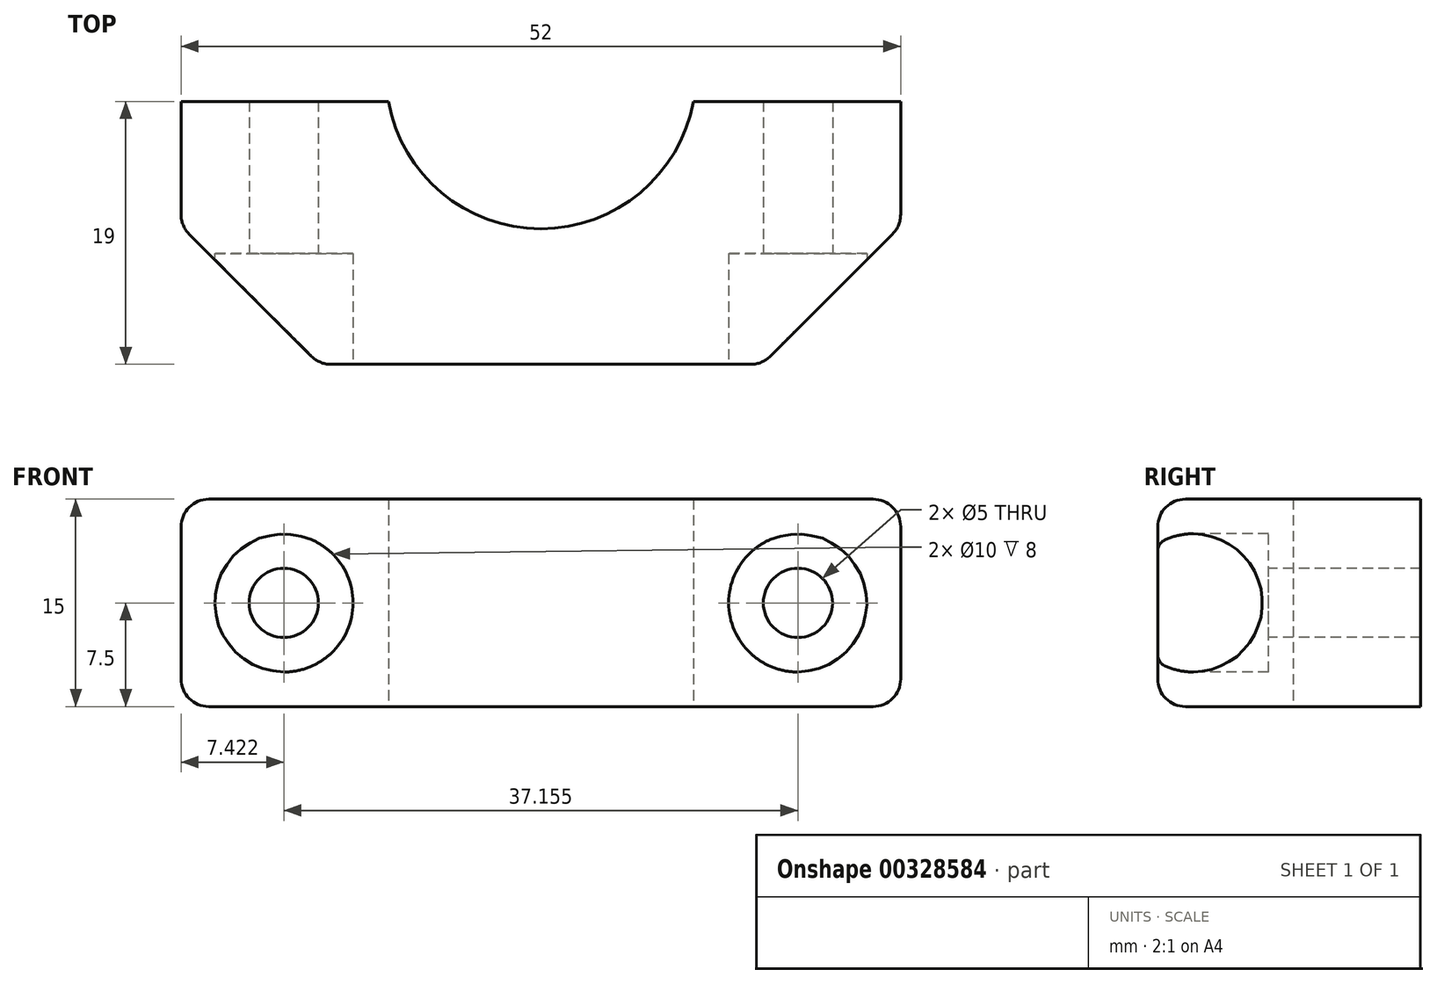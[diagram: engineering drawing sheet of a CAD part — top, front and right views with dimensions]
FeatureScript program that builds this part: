
annotation { "Feature Type Name" : "Feature", "Feature Type Description" : "" }
export const myFeature = defineFeature(function(context is Context, id is Id, definition is map)
    precondition{}
    {
        {
            var Q0;
            Q0=qCreatedBy(makeId("Top.planeOp"),FACE);
            var sketch = newSketch(context, id + "F0", { "sketchPlane" : qUnion([Q0])});
            skLineSegment(sketch, "E0.bottom", {"start": v(21, -10) * mm, "end": v(-21, -10) * mm});
            skLineSegment(sketch, "E0.top", {"start": v(21, 10) * mm, "end": v(-21, 10) * mm});
            skLineSegment(sketch, "E0.left", {"start": v(21, -10) * mm, "end": v(21, 10) * mm});
            skLineSegment(sketch, "E0.right", {"start": v(-21, -10) * mm, "end": v(-21, 10) * mm});
            skPoint(sketch, "E0.middle", {"position": v(0, 0) * mm});
            skCircle(sketch, "E1", {"center": v(0, 11) * mm, "radius": 11.2 * mm});
            skPoint(sketch, "E1.centerSnap0", {"position": v(0, 10) * mm});
            skSolve(sketch);
        }
        {
            var Q0;
            Q0=makeQuery(id+"F0.imprint","IMPRINT",FACE,{"disambiguationData":[TD([[makeQuery(id+"F0.imprint","IMPRINT",EDGE,{"derivedFrom":sQuery(id+"F0.wireOp",EDGE,"E0.bottom")}),-1.0]])]});
            extrude(context, id + "F1", {"entities" : qUnion([Q0]), "depth" : 15 * mm});
        }
        {
            var Q0;
            Q0=makeQuery(id+"F1.opExtrude","SWEPT_FACE",FACE,{"disambiguationData":[OSD([sQuery(id+"F0.wireOp",EDGE,"E0.left")])]});
            extrude(context, id + "F2", {"entities" : qUnion([Q0]), "operationType" : NewBodyOperationType.ADD, "depth" : 5 * mm});
        }
        {
            var Q0;
            Q0=makeQuery(id+"F1.opExtrude","SWEPT_FACE",FACE,{"disambiguationData":[OSD([sQuery(id+"F0.wireOp",EDGE,"E0.right")])]});
            extrude(context, id + "F3", {"entities" : qUnion([Q0]), "operationType" : NewBodyOperationType.ADD, "depth" : 5 * mm});
        }
        {
            var Q0;
            {var subQ0=sQuery(id+"F0.wireOp",EDGE,"E0.bottom");Q0=makeQuery(id+"F3.boolean.opBoolean","MERGE",FACE,{"derivedFrom":[makeQuery(id+"F2.boolean.opBoolean","MERGE",FACE,{"derivedFrom":[makeQuery(id+"F1.opExtrude","SWEPT_FACE",FACE,{"disambiguationData":[OSD([subQ0])]}),makeQuery(id+"F2.opExtrude","SWEPT_FACE",FACE,{"disambiguationData":[OSD([subQ0,sQuery(id+"F0.wireOp",EDGE,"E0.left")])]})]}),makeQuery(id+"F3.opExtrude","SWEPT_FACE",FACE,{"disambiguationData":[OSD([subQ0,sQuery(id+"F0.wireOp",EDGE,"E0.right")])]})]});}
            var sketch = newSketch(context, id + "F4", { "sketchPlane" : qUnion([Q0])});
            skLineSegment(sketch, "E2.0", {"start": v(11.16, 15) * mm, "end": v(11.16, 0) * mm});
            skLineSegment(sketch, "E3.0", {"start": v(-11.16, 15) * mm, "end": v(-11.16, 0) * mm});
            skLineSegment(sketch, "E4", {"start": v(26, 7.5) * mm, "end": v(11.16, 7.5) * mm});
            skLineSegment(sketch, "E5", {"start": v(11.16, 7.5) * mm, "end": v(-11.16, 7.5) * mm});
            skLineSegment(sketch, "E6", {"start": v(-11.16, 7.5) * mm, "end": v(-26, 7.5) * mm});
            skPoint(sketch, "E7", {"position": v(18.58, 7.5) * mm});
            skPoint(sketch, "E8", {"position": v(-18.58, 7.5) * mm});
            skSolve(sketch);
        }
        {
            var Q0;
            Q0=sQuery(id+"F4.wireOp",VERTEX,"E7");
            var Q1;
            Q1=sQuery(id+"F4.wireOp",VERTEX,"E8");
            var Q2;
            Q2=makeQuery(id+"F1.opExtrude","SWEPT_BODY",BODY,{"disambiguationData":[OSD([sQuery(id+"F0.wireOp",EDGE,"E0.bottom"),sQuery(id+"F0.wireOp",EDGE,"E0.top"),sQuery(id+"F0.wireOp",EDGE,"E0.left"),sQuery(id+"F0.wireOp",EDGE,"E0.right"),sQuery(id+"F0.wireOp",EDGE,"E1")])]});
            hole(context, id + "F5", {"style" : HoleStyle.C_BORE, "endStyle" : HoleEndStyle.THROUGH, "holeDiameter" : 5 * mm, "cBoreDiameter" : 10 * mm, "cBoreDepth" : 8 * mm, "tappedDepth" : 12 * mm, "tapClearance" : 3, "locations" : qUnion([Q0, Q1]), "scope" : qUnion([Q2])});
        }
        {
            var Q0;
            Q0=makeQuery(id+"F2.opExtrude","CAP_EDGE",EDGE,{"disambiguationData":[OSD([sQuery(id+"F0.wireOp",EDGE,"E0.bottom"),sQuery(id+"F0.wireOp",EDGE,"E0.left")])],"isStart":false});
            var Q1;
            Q1=makeQuery(id+"F3.opExtrude","CAP_EDGE",EDGE,{"disambiguationData":[OSD([sQuery(id+"F0.wireOp",EDGE,"E0.bottom"),sQuery(id+"F0.wireOp",EDGE,"E0.right")])],"isStart":false});
            chamfer(context, id + "F6", {"entities" : qUnion([Q0, Q1]), "width" : 10 * mm, "tangentPropagation" : true});
        }
        {
            var Q0;
            {var subQ0=sQuery(id+"F0.wireOp",EDGE,"E0.right");var subQ1=sQuery(id+"F0.wireOp",EDGE,"E0.bottom");var subQ2=sQuery(id+"F0.wireOp",EDGE,"E0.left");Q0=makeQuery(id+"F3.boolean.opBoolean","MERGE",EDGE,{"derivedFrom":[makeQuery(id+"F2.boolean.opBoolean","MERGE",EDGE,{"derivedFrom":[makeQuery(id+"F1.opExtrude","CAP_EDGE",EDGE,{"disambiguationData":[OSD([subQ1])],"isStart":false}),makeQuery(id+"F2.opExtrude","SWEPT_EDGE",EDGE,{"disambiguationData":[OSD([subQ1,subQ2]),TDD([makeQuery(id+"F1.opExtrude","CAP_VERTEX",VERTEX,{"disambiguationData":[OSD([subQ1,subQ2])],"isStart":false})])]})]}),makeQuery(id+"F3.opExtrude","SWEPT_EDGE",EDGE,{"disambiguationData":[OSD([subQ1,subQ0]),TDD([makeQuery(id+"F1.opExtrude","CAP_VERTEX",VERTEX,{"disambiguationData":[OSD([subQ1,subQ0])],"isStart":false})])]})]});}
            var Q1;
            {var subQ0=sQuery(id+"F0.wireOp",EDGE,"E0.right");var subQ1=sQuery(id+"F0.wireOp",EDGE,"E0.left");var subQ2=sQuery(id+"F0.wireOp",EDGE,"E0.bottom");Q1=makeQuery(id+"F6.opChamfer","BLEND_EDGE",EDGE,{"blendedFrom":[makeQuery(id+"F2.opExtrude","CAP_EDGE",EDGE,{"disambiguationData":[OSD([subQ2,subQ1])],"isStart":false}),makeQuery(id+"F3.boolean.opBoolean","MERGE",FACE,{"derivedFrom":[makeQuery(id+"F2.boolean.opBoolean","MERGE",FACE,{"derivedFrom":[makeQuery(id+"F1.opExtrude","CAP_FACE",FACE,{"disambiguationData":[OSD([subQ2,sQuery(id+"F0.wireOp",EDGE,"E0.top"),subQ1,subQ0,sQuery(id+"F0.wireOp",EDGE,"E1")])],"isStart":false}),makeQuery(id+"F2.opExtrude","SWEPT_FACE",FACE,{"disambiguationData":[OSD([subQ1]),TDD([makeQuery(id+"F1.opExtrude","CAP_EDGE",EDGE,{"disambiguationData":[OSD([subQ1])],"isStart":false})])]})]}),makeQuery(id+"F3.opExtrude","SWEPT_FACE",FACE,{"disambiguationData":[OSD([subQ0]),TDD([makeQuery(id+"F1.opExtrude","CAP_EDGE",EDGE,{"disambiguationData":[OSD([subQ0])],"isStart":false})])]})]})],"blendedInto":[makeQuery(id+"F3.boolean.opBoolean","MERGE",FACE,{"derivedFrom":[makeQuery(id+"F2.boolean.opBoolean","MERGE",FACE,{"derivedFrom":[makeQuery(id+"F1.opExtrude","CAP_FACE",FACE,{"disambiguationData":[OSD([subQ2,sQuery(id+"F0.wireOp",EDGE,"E0.top"),subQ1,subQ0,sQuery(id+"F0.wireOp",EDGE,"E1")])],"isStart":false}),makeQuery(id+"F2.opExtrude","SWEPT_FACE",FACE,{"disambiguationData":[OSD([subQ1]),TDD([makeQuery(id+"F1.opExtrude","CAP_EDGE",EDGE,{"disambiguationData":[OSD([subQ1])],"isStart":false})])]})]}),makeQuery(id+"F3.opExtrude","SWEPT_FACE",FACE,{"disambiguationData":[OSD([subQ0]),TDD([makeQuery(id+"F1.opExtrude","CAP_EDGE",EDGE,{"disambiguationData":[OSD([subQ0])],"isStart":false})])]})]})]});}
            var Q2;
            {var subQ0=sQuery(id+"F0.wireOp",EDGE,"E0.right");Q2=makeQuery(id+"F3.opExtrude","CAP_EDGE",EDGE,{"disambiguationData":[OSD([subQ0]),TDD([makeQuery(id+"F1.opExtrude","CAP_EDGE",EDGE,{"disambiguationData":[OSD([subQ0])],"isStart":false})])],"isStart":false});}
            var Q3;
            {var subQ0=sQuery(id+"F0.wireOp",EDGE,"E0.left");Q3=makeQuery(id+"F2.opExtrude","CAP_EDGE",EDGE,{"disambiguationData":[OSD([subQ0]),TDD([makeQuery(id+"F1.opExtrude","CAP_EDGE",EDGE,{"disambiguationData":[OSD([subQ0])],"isStart":false})])],"isStart":false});}
            var Q4;
            {var subQ0=sQuery(id+"F0.wireOp",EDGE,"E0.right");var subQ1=sQuery(id+"F0.wireOp",EDGE,"E0.left");var subQ2=sQuery(id+"F0.wireOp",EDGE,"E0.bottom");Q4=makeQuery(id+"F6.opChamfer","BLEND_EDGE",EDGE,{"blendedFrom":[makeQuery(id+"F3.opExtrude","CAP_EDGE",EDGE,{"disambiguationData":[OSD([subQ2,subQ0])],"isStart":false}),makeQuery(id+"F3.boolean.opBoolean","MERGE",FACE,{"derivedFrom":[makeQuery(id+"F2.boolean.opBoolean","MERGE",FACE,{"derivedFrom":[makeQuery(id+"F1.opExtrude","CAP_FACE",FACE,{"disambiguationData":[OSD([subQ2,sQuery(id+"F0.wireOp",EDGE,"E0.top"),subQ1,subQ0,sQuery(id+"F0.wireOp",EDGE,"E1")])],"isStart":false}),makeQuery(id+"F2.opExtrude","SWEPT_FACE",FACE,{"disambiguationData":[OSD([subQ1]),TDD([makeQuery(id+"F1.opExtrude","CAP_EDGE",EDGE,{"disambiguationData":[OSD([subQ1])],"isStart":false})])]})]}),makeQuery(id+"F3.opExtrude","SWEPT_FACE",FACE,{"disambiguationData":[OSD([subQ0]),TDD([makeQuery(id+"F1.opExtrude","CAP_EDGE",EDGE,{"disambiguationData":[OSD([subQ0])],"isStart":false})])]})]})],"blendedInto":[makeQuery(id+"F3.boolean.opBoolean","MERGE",FACE,{"derivedFrom":[makeQuery(id+"F2.boolean.opBoolean","MERGE",FACE,{"derivedFrom":[makeQuery(id+"F1.opExtrude","CAP_FACE",FACE,{"disambiguationData":[OSD([subQ2,sQuery(id+"F0.wireOp",EDGE,"E0.top"),subQ1,subQ0,sQuery(id+"F0.wireOp",EDGE,"E1")])],"isStart":false}),makeQuery(id+"F2.opExtrude","SWEPT_FACE",FACE,{"disambiguationData":[OSD([subQ1]),TDD([makeQuery(id+"F1.opExtrude","CAP_EDGE",EDGE,{"disambiguationData":[OSD([subQ1])],"isStart":false})])]})]}),makeQuery(id+"F3.opExtrude","SWEPT_FACE",FACE,{"disambiguationData":[OSD([subQ0]),TDD([makeQuery(id+"F1.opExtrude","CAP_EDGE",EDGE,{"disambiguationData":[OSD([subQ0])],"isStart":false})])]})]})]});}
            var Q5;
            {var subQ0=sQuery(id+"F0.wireOp",EDGE,"E0.right");var subQ1=sQuery(id+"F0.wireOp",EDGE,"E0.left");var subQ2=sQuery(id+"F0.wireOp",EDGE,"E0.bottom");Q5=makeQuery(id+"F6.opChamfer","BLEND_EDGE",EDGE,{"blendedFrom":[makeQuery(id+"F2.opExtrude","CAP_EDGE",EDGE,{"disambiguationData":[OSD([subQ2,subQ1])],"isStart":false}),makeQuery(id+"F3.boolean.opBoolean","MERGE",FACE,{"derivedFrom":[makeQuery(id+"F2.boolean.opBoolean","MERGE",FACE,{"derivedFrom":[makeQuery(id+"F1.opExtrude","CAP_FACE",FACE,{"disambiguationData":[OSD([subQ2,sQuery(id+"F0.wireOp",EDGE,"E0.top"),subQ1,subQ0,sQuery(id+"F0.wireOp",EDGE,"E1")])],"isStart":true}),makeQuery(id+"F2.opExtrude","SWEPT_FACE",FACE,{"disambiguationData":[OSD([subQ1]),TDD([makeQuery(id+"F1.opExtrude","CAP_EDGE",EDGE,{"disambiguationData":[OSD([subQ1])],"isStart":true})])]})]}),makeQuery(id+"F3.opExtrude","SWEPT_FACE",FACE,{"disambiguationData":[OSD([subQ0]),TDD([makeQuery(id+"F1.opExtrude","CAP_EDGE",EDGE,{"disambiguationData":[OSD([subQ0])],"isStart":true})])]})]})],"blendedInto":[makeQuery(id+"F3.boolean.opBoolean","MERGE",FACE,{"derivedFrom":[makeQuery(id+"F2.boolean.opBoolean","MERGE",FACE,{"derivedFrom":[makeQuery(id+"F1.opExtrude","CAP_FACE",FACE,{"disambiguationData":[OSD([subQ2,sQuery(id+"F0.wireOp",EDGE,"E0.top"),subQ1,subQ0,sQuery(id+"F0.wireOp",EDGE,"E1")])],"isStart":true}),makeQuery(id+"F2.opExtrude","SWEPT_FACE",FACE,{"disambiguationData":[OSD([subQ1]),TDD([makeQuery(id+"F1.opExtrude","CAP_EDGE",EDGE,{"disambiguationData":[OSD([subQ1])],"isStart":true})])]})]}),makeQuery(id+"F3.opExtrude","SWEPT_FACE",FACE,{"disambiguationData":[OSD([subQ0]),TDD([makeQuery(id+"F1.opExtrude","CAP_EDGE",EDGE,{"disambiguationData":[OSD([subQ0])],"isStart":true})])]})]})]});}
            var Q6;
            {var subQ0=sQuery(id+"F0.wireOp",EDGE,"E0.right");var subQ1=sQuery(id+"F0.wireOp",EDGE,"E0.bottom");var subQ2=sQuery(id+"F0.wireOp",EDGE,"E0.left");Q6=makeQuery(id+"F3.boolean.opBoolean","MERGE",EDGE,{"derivedFrom":[makeQuery(id+"F2.boolean.opBoolean","MERGE",EDGE,{"derivedFrom":[makeQuery(id+"F1.opExtrude","CAP_EDGE",EDGE,{"disambiguationData":[OSD([subQ1])],"isStart":true}),makeQuery(id+"F2.opExtrude","SWEPT_EDGE",EDGE,{"disambiguationData":[OSD([subQ1,subQ2]),TDD([makeQuery(id+"F1.opExtrude","CAP_VERTEX",VERTEX,{"disambiguationData":[OSD([subQ1,subQ2])],"isStart":true})])]})]}),makeQuery(id+"F3.opExtrude","SWEPT_EDGE",EDGE,{"disambiguationData":[OSD([subQ1,subQ0]),TDD([makeQuery(id+"F1.opExtrude","CAP_VERTEX",VERTEX,{"disambiguationData":[OSD([subQ1,subQ0])],"isStart":true})])]})]});}
            var Q7;
            {var subQ0=sQuery(id+"F0.wireOp",EDGE,"E0.right");var subQ1=sQuery(id+"F0.wireOp",EDGE,"E0.left");var subQ2=sQuery(id+"F0.wireOp",EDGE,"E0.bottom");Q7=makeQuery(id+"F6.opChamfer","BLEND_EDGE",EDGE,{"blendedFrom":[makeQuery(id+"F3.opExtrude","CAP_EDGE",EDGE,{"disambiguationData":[OSD([subQ2,subQ0])],"isStart":false}),makeQuery(id+"F3.boolean.opBoolean","MERGE",FACE,{"derivedFrom":[makeQuery(id+"F2.boolean.opBoolean","MERGE",FACE,{"derivedFrom":[makeQuery(id+"F1.opExtrude","CAP_FACE",FACE,{"disambiguationData":[OSD([subQ2,sQuery(id+"F0.wireOp",EDGE,"E0.top"),subQ1,subQ0,sQuery(id+"F0.wireOp",EDGE,"E1")])],"isStart":true}),makeQuery(id+"F2.opExtrude","SWEPT_FACE",FACE,{"disambiguationData":[OSD([subQ1]),TDD([makeQuery(id+"F1.opExtrude","CAP_EDGE",EDGE,{"disambiguationData":[OSD([subQ1])],"isStart":true})])]})]}),makeQuery(id+"F3.opExtrude","SWEPT_FACE",FACE,{"disambiguationData":[OSD([subQ0]),TDD([makeQuery(id+"F1.opExtrude","CAP_EDGE",EDGE,{"disambiguationData":[OSD([subQ0])],"isStart":true})])]})]})],"blendedInto":[makeQuery(id+"F3.boolean.opBoolean","MERGE",FACE,{"derivedFrom":[makeQuery(id+"F2.boolean.opBoolean","MERGE",FACE,{"derivedFrom":[makeQuery(id+"F1.opExtrude","CAP_FACE",FACE,{"disambiguationData":[OSD([subQ2,sQuery(id+"F0.wireOp",EDGE,"E0.top"),subQ1,subQ0,sQuery(id+"F0.wireOp",EDGE,"E1")])],"isStart":true}),makeQuery(id+"F2.opExtrude","SWEPT_FACE",FACE,{"disambiguationData":[OSD([subQ1]),TDD([makeQuery(id+"F1.opExtrude","CAP_EDGE",EDGE,{"disambiguationData":[OSD([subQ1])],"isStart":true})])]})]}),makeQuery(id+"F3.opExtrude","SWEPT_FACE",FACE,{"disambiguationData":[OSD([subQ0]),TDD([makeQuery(id+"F1.opExtrude","CAP_EDGE",EDGE,{"disambiguationData":[OSD([subQ0])],"isStart":true})])]})]})]});}
            var Q8;
            {var subQ0=sQuery(id+"F0.wireOp",EDGE,"E0.left");Q8=makeQuery(id+"F2.opExtrude","CAP_EDGE",EDGE,{"disambiguationData":[OSD([subQ0]),TDD([makeQuery(id+"F1.opExtrude","CAP_EDGE",EDGE,{"disambiguationData":[OSD([subQ0])],"isStart":true})])],"isStart":false});}
            var Q9;
            {var subQ0=sQuery(id+"F0.wireOp",EDGE,"E0.right");Q9=makeQuery(id+"F3.opExtrude","CAP_EDGE",EDGE,{"disambiguationData":[OSD([subQ0]),TDD([makeQuery(id+"F1.opExtrude","CAP_EDGE",EDGE,{"disambiguationData":[OSD([subQ0])],"isStart":true})])],"isStart":false});}
            var Q10;
            {var subQ0=sQuery(id+"F0.wireOp",EDGE,"E0.bottom");var subQ1=sQuery(id+"F0.wireOp",EDGE,"E0.left");Q10=makeQuery(id+"F6.opChamfer","BLEND_EDGE",EDGE,{"disambiguationData":[OD(1.0)],"blendedFrom":[makeQuery(id+"F2.opExtrude","CAP_EDGE",EDGE,{"disambiguationData":[OSD([subQ0,subQ1])],"isStart":false}),makeQuery(id+"F3.boolean.opBoolean","MERGE",FACE,{"derivedFrom":[makeQuery(id+"F2.boolean.opBoolean","MERGE",FACE,{"derivedFrom":[makeQuery(id+"F1.opExtrude","SWEPT_FACE",FACE,{"disambiguationData":[OSD([subQ0])]}),makeQuery(id+"F2.opExtrude","SWEPT_FACE",FACE,{"disambiguationData":[OSD([subQ0,subQ1])]})]}),makeQuery(id+"F3.opExtrude","SWEPT_FACE",FACE,{"disambiguationData":[OSD([subQ0,sQuery(id+"F0.wireOp",EDGE,"E0.right")])]})]})],"blendedInto":[makeQuery(id+"F3.boolean.opBoolean","MERGE",FACE,{"derivedFrom":[makeQuery(id+"F2.boolean.opBoolean","MERGE",FACE,{"derivedFrom":[makeQuery(id+"F1.opExtrude","SWEPT_FACE",FACE,{"disambiguationData":[OSD([subQ0])]}),makeQuery(id+"F2.opExtrude","SWEPT_FACE",FACE,{"disambiguationData":[OSD([subQ0,subQ1])]})]}),makeQuery(id+"F3.opExtrude","SWEPT_FACE",FACE,{"disambiguationData":[OSD([subQ0,sQuery(id+"F0.wireOp",EDGE,"E0.right")])]})]})]});}
            var Q11;
            {var subQ0=sQuery(id+"F0.wireOp",EDGE,"E0.bottom");var subQ1=sQuery(id+"F0.wireOp",EDGE,"E0.left");Q11=makeQuery(id+"F6.opChamfer","BLEND_EDGE",EDGE,{"disambiguationData":[OD(0.0)],"blendedFrom":[makeQuery(id+"F2.opExtrude","CAP_EDGE",EDGE,{"disambiguationData":[OSD([subQ0,subQ1])],"isStart":false}),makeQuery(id+"F3.boolean.opBoolean","MERGE",FACE,{"derivedFrom":[makeQuery(id+"F2.boolean.opBoolean","MERGE",FACE,{"derivedFrom":[makeQuery(id+"F1.opExtrude","SWEPT_FACE",FACE,{"disambiguationData":[OSD([subQ0])]}),makeQuery(id+"F2.opExtrude","SWEPT_FACE",FACE,{"disambiguationData":[OSD([subQ0,subQ1])]})]}),makeQuery(id+"F3.opExtrude","SWEPT_FACE",FACE,{"disambiguationData":[OSD([subQ0,sQuery(id+"F0.wireOp",EDGE,"E0.right")])]})]})],"blendedInto":[makeQuery(id+"F3.boolean.opBoolean","MERGE",FACE,{"derivedFrom":[makeQuery(id+"F2.boolean.opBoolean","MERGE",FACE,{"derivedFrom":[makeQuery(id+"F1.opExtrude","SWEPT_FACE",FACE,{"disambiguationData":[OSD([subQ0])]}),makeQuery(id+"F2.opExtrude","SWEPT_FACE",FACE,{"disambiguationData":[OSD([subQ0,subQ1])]})]}),makeQuery(id+"F3.opExtrude","SWEPT_FACE",FACE,{"disambiguationData":[OSD([subQ0,sQuery(id+"F0.wireOp",EDGE,"E0.right")])]})]})]});}
            var Q12;
            {var subQ0=sQuery(id+"F0.wireOp",EDGE,"E0.right");var subQ1=sQuery(id+"F0.wireOp",EDGE,"E0.bottom");Q12=makeQuery(id+"F6.opChamfer","BLEND_EDGE",EDGE,{"disambiguationData":[OD(0.0)],"blendedFrom":[makeQuery(id+"F3.opExtrude","CAP_EDGE",EDGE,{"disambiguationData":[OSD([subQ1,subQ0])],"isStart":false}),makeQuery(id+"F3.boolean.opBoolean","MERGE",FACE,{"derivedFrom":[makeQuery(id+"F2.boolean.opBoolean","MERGE",FACE,{"derivedFrom":[makeQuery(id+"F1.opExtrude","SWEPT_FACE",FACE,{"disambiguationData":[OSD([subQ1])]}),makeQuery(id+"F2.opExtrude","SWEPT_FACE",FACE,{"disambiguationData":[OSD([subQ1,sQuery(id+"F0.wireOp",EDGE,"E0.left")])]})]}),makeQuery(id+"F3.opExtrude","SWEPT_FACE",FACE,{"disambiguationData":[OSD([subQ1,subQ0])]})]})],"blendedInto":[makeQuery(id+"F3.boolean.opBoolean","MERGE",FACE,{"derivedFrom":[makeQuery(id+"F2.boolean.opBoolean","MERGE",FACE,{"derivedFrom":[makeQuery(id+"F1.opExtrude","SWEPT_FACE",FACE,{"disambiguationData":[OSD([subQ1])]}),makeQuery(id+"F2.opExtrude","SWEPT_FACE",FACE,{"disambiguationData":[OSD([subQ1,sQuery(id+"F0.wireOp",EDGE,"E0.left")])]})]}),makeQuery(id+"F3.opExtrude","SWEPT_FACE",FACE,{"disambiguationData":[OSD([subQ1,subQ0])]})]})]});}
            var Q13;
            {var subQ0=sQuery(id+"F0.wireOp",EDGE,"E0.right");var subQ1=sQuery(id+"F0.wireOp",EDGE,"E0.bottom");Q13=makeQuery(id+"F6.opChamfer","BLEND_EDGE",EDGE,{"disambiguationData":[OD(1.0)],"blendedFrom":[makeQuery(id+"F3.opExtrude","CAP_EDGE",EDGE,{"disambiguationData":[OSD([subQ1,subQ0])],"isStart":false}),makeQuery(id+"F3.boolean.opBoolean","MERGE",FACE,{"derivedFrom":[makeQuery(id+"F2.boolean.opBoolean","MERGE",FACE,{"derivedFrom":[makeQuery(id+"F1.opExtrude","SWEPT_FACE",FACE,{"disambiguationData":[OSD([subQ1])]}),makeQuery(id+"F2.opExtrude","SWEPT_FACE",FACE,{"disambiguationData":[OSD([subQ1,sQuery(id+"F0.wireOp",EDGE,"E0.left")])]})]}),makeQuery(id+"F3.opExtrude","SWEPT_FACE",FACE,{"disambiguationData":[OSD([subQ1,subQ0])]})]})],"blendedInto":[makeQuery(id+"F3.boolean.opBoolean","MERGE",FACE,{"derivedFrom":[makeQuery(id+"F2.boolean.opBoolean","MERGE",FACE,{"derivedFrom":[makeQuery(id+"F1.opExtrude","SWEPT_FACE",FACE,{"disambiguationData":[OSD([subQ1])]}),makeQuery(id+"F2.opExtrude","SWEPT_FACE",FACE,{"disambiguationData":[OSD([subQ1,sQuery(id+"F0.wireOp",EDGE,"E0.left")])]})]}),makeQuery(id+"F3.opExtrude","SWEPT_FACE",FACE,{"disambiguationData":[OSD([subQ1,subQ0])]})]})]});}
            var Q14;
            {var subQ0=sQuery(id+"F0.wireOp",EDGE,"E0.left");Q14=makeQuery(id+"F6.opChamfer","BLEND_EDGE",EDGE,{"blendedFrom":[makeQuery(id+"F2.opExtrude","CAP_EDGE",EDGE,{"disambiguationData":[OSD([sQuery(id+"F0.wireOp",EDGE,"E0.bottom"),subQ0])],"isStart":false}),makeQuery(id+"F2.opExtrude","CAP_FACE",FACE,{"disambiguationData":[OSD([subQ0])],"isStart":false})],"blendedInto":[makeQuery(id+"F2.opExtrude","CAP_FACE",FACE,{"disambiguationData":[OSD([subQ0])],"isStart":false})]});}
            var Q15;
            {var subQ0=sQuery(id+"F0.wireOp",EDGE,"E0.right");Q15=makeQuery(id+"F6.opChamfer","BLEND_EDGE",EDGE,{"blendedFrom":[makeQuery(id+"F3.opExtrude","CAP_EDGE",EDGE,{"disambiguationData":[OSD([sQuery(id+"F0.wireOp",EDGE,"E0.bottom"),subQ0])],"isStart":false}),makeQuery(id+"F3.opExtrude","CAP_FACE",FACE,{"disambiguationData":[OSD([subQ0])],"isStart":false})],"blendedInto":[makeQuery(id+"F3.opExtrude","CAP_FACE",FACE,{"disambiguationData":[OSD([subQ0])],"isStart":false})]});}
            fillet(context, id + "F7", {"entities" : qUnion([Q0, Q1, Q2, Q3, Q4, Q5, Q6, Q7, Q8, Q9, Q10, Q11, Q12, Q13, Q14, Q15]), "radius" : 2 * mm, "tangentPropagation" : true, "allowEdgeOverflow" : false});
        }
        {
            var Q0;
            {var subQ0=sQuery(id+"F0.wireOp",EDGE,"E0.right");var subQ1=sQuery(id+"F0.wireOp",EDGE,"E0.top");Q0=makeQuery(id+"F3.boolean.opBoolean","MERGE",FACE,{"derivedFrom":[makeQuery(id+"F1.opExtrude","SWEPT_FACE",FACE,{"disambiguationData":[OSD([subQ1]),TDD([makeQuery(id+"F0.imprint","IMPRINT",EDGE,{"disambiguationData":[TD([[makeQuery(id+"F0.imprint","INTERSECT",VERTEX,{"derivedFrom":[subQ1,subQ0]}),1.0]])],"derivedFrom":subQ1})])]}),makeQuery(id+"F3.opExtrude","SWEPT_FACE",FACE,{"disambiguationData":[OSD([subQ1,subQ0])]})]});}
            var sketch = newSketch(context, id + "F8", { "sketchPlane" : qUnion([Q0])});
            skLineSegment(sketch, "E9.bottom", {"start": v(26, 0) * mm, "end": v(-28.7, 0) * mm});
            skLineSegment(sketch, "E9.top", {"start": v(26, 16.13) * mm, "end": v(-28.7, 16.13) * mm});
            skLineSegment(sketch, "E9.left", {"start": v(26, 0) * mm, "end": v(26, 16.13) * mm});
            skLineSegment(sketch, "E9.right", {"start": v(-28.7, 0) * mm, "end": v(-28.7, 16.13) * mm});
            skSolve(sketch);
        }
        {
            var Q0;
            Q0 = qSketchRegion(id + "F8", true);
            extrude(context, id + "F9", {"entities" : qUnion([Q0]), "operationType" : NewBodyOperationType.REMOVE, "oppositeDirection" : true, "depth" : 1 * mm});
        }
    });
